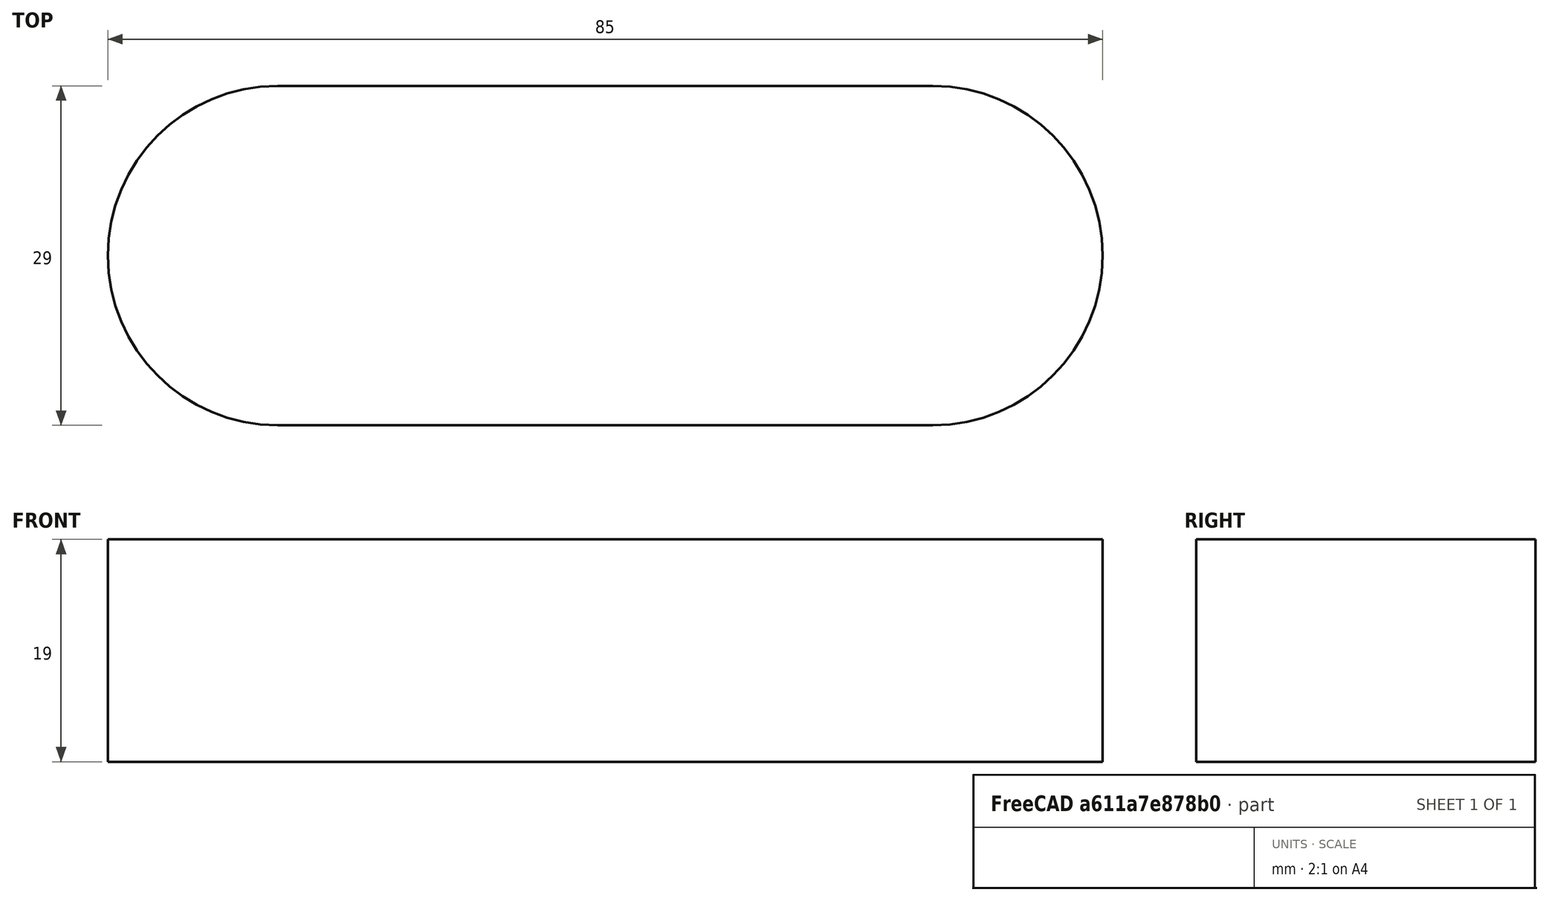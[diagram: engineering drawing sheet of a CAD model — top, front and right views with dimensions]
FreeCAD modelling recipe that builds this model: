
FCSTD DOCUMENT  (FreeCAD 0.22R36183 (Git))
Label: UST-E32 WHITE 2M
License: All rights reserved
LicenseURL: http://en.wikipedia.org/wiki/All_rights_reserved
objects: Sketcher::SketchObject×1, PartDesign::Pad×1, PartDesign::Body×1
note: 4 computed .brp shape members not serialized (recipe doc carries the construction recipe); baked Part::Feature solids carry a one-line shape summary decoded from their .brp

FEATURE [Sketcher::SketchObject] Sketch  label="base"
  FullyConstrained = true
  MapMode = 5
  Support = -> [XY_Plane]
  sketch-geometry (6):
    g0: ArcOfCircle CenterX=-28 CenterY=0 CenterZ=0 NormalX=0 NormalY=0 NormalZ=1 AngleXU=0 Radius=14.5 StartAngle=1.5708 EndAngle=4.71239
    g1: ArcOfCircle CenterX=28 CenterY=0 CenterZ=0 NormalX=0 NormalY=0 NormalZ=1 AngleXU=0 Radius=14.5 StartAngle=4.71239 EndAngle=7.85398
    g2: LineSegment StartX=-28 StartY=-14.5 StartZ=0 EndX=28 EndY=-14.5 EndZ=0
    g3: LineSegment StartX=28 StartY=14.5 StartZ=0 EndX=-28 EndY=14.5 EndZ=0
    g4: GeomPoint X=-42.5 Y=0 Z=0
    g5: GeomPoint X=42.5 Y=0 Z=0
  constraints (13):
    c: Tangent(g0,g2) = -1.5708
    c: Tangent(g2,g1) = -1.5708
    c: Tangent(g1,g3) = -1.5708
    c: Tangent(g3,g0) = -1.5708
    c: Equal(g0,g1)
    c: PointOnObject(g0,g-1)
    c: Symmetric(g0,g1,g-2)
    c: PointOnObject(g4,g0)
    c: PointOnObject(g5,g1)
    c: PointOnObject(g5,g-1)
    c: PointOnObject(g4,g-1)
    c: DistanceX(g4,g5) = 85
    c: DistanceY(g1,g1) = 29
FEATURE [PartDesign::Pad] Pad
  Direction = (0,0,1)
  Length = 19
  Length2 = 10
  Profile = -> Sketch
  ReferenceAxis = -> Sketch [N_Axis]
  Suppressed = false
  Type = 0
FEATURE [PartDesign::Body] Body
  Group = -> [Sketch,Pad]
  Origin = -> Origin
  Tip = -> Pad
